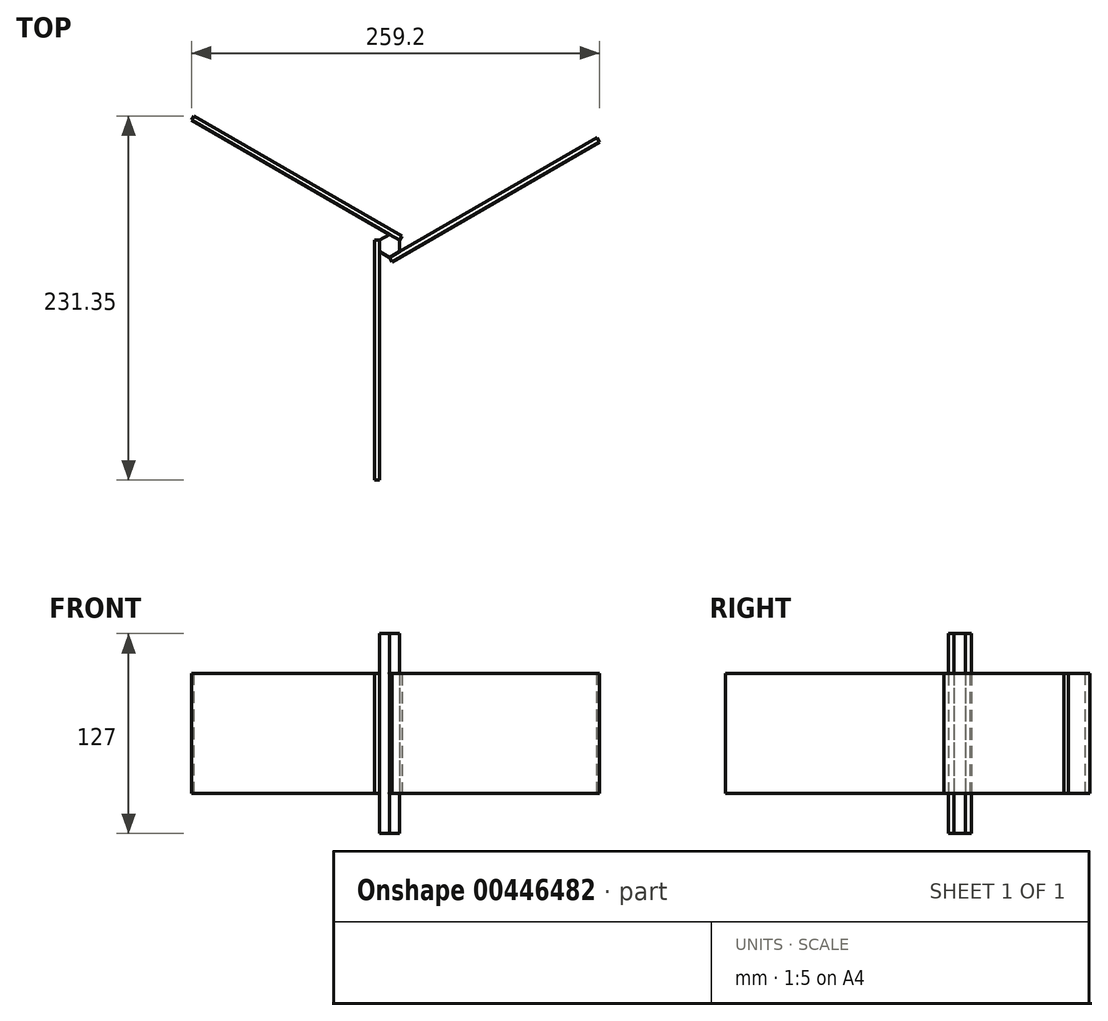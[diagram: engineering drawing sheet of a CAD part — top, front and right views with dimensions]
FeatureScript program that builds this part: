
annotation { "Feature Type Name" : "Feature", "Feature Type Description" : "" }
export const myFeature = defineFeature(function(context is Context, id is Id, definition is map)
    precondition{}
    {
        {
            var Q0;
            Q0=qCreatedBy(makeId("Top.planeOp"),FACE);
            var sketch = newSketch(context, id + "F0", { "sketchPlane" : qUnion([Q0])});
            skCircle(sketch, "E0.cCircle", {"center": v(0, 0) * mm, "radius": 6.35 * mm, "construction": true});
            skLineSegment(sketch, "E0.0", {"start": v(6.35, 3.67) * mm, "end": v(6.35, -3.67) * mm});
            skLineSegment(sketch, "E0.1", {"start": v(6.35, -3.67) * mm, "end": v(0, -7.33) * mm});
            skLineSegment(sketch, "E0.2", {"start": v(0, -7.33) * mm, "end": v(-6.35, -3.67) * mm});
            skLineSegment(sketch, "E0.3", {"start": v(-6.35, -3.67) * mm, "end": v(-6.35, 3.67) * mm});
            skLineSegment(sketch, "E0.4", {"start": v(-6.35, 3.67) * mm, "end": v(0, 7.33) * mm});
            skLineSegment(sketch, "E0.5", {"start": v(0, 7.33) * mm, "end": v(6.35, 3.67) * mm});
            skPoint(sketch, "E0.0.midPoint", {"position": v(6.35, 0) * mm});
            skSolve(sketch);
        }
        {
            var Q0;
            Q0=makeQuery(id+"F0.imprint","IMPRINT",FACE,{"disambiguationData":[TD([[makeQuery(id+"F0.imprint","IMPRINT",EDGE,{"derivedFrom":sQuery(id+"F0.wireOp",EDGE,"E0.0")}),-1.0]])]});
            extrude(context, id + "F1", {"entities" : qUnion([Q0]), "depth" : 127 * mm, "symmetric" : true});
        }
        {
            var Q0;
            Q0=makeQuery(id+"F1.opExtrude","SWEPT_FACE",FACE,{"disambiguationData":[OSD([sQuery(id+"F0.wireOp",EDGE,"E0.1")])]});
            var sketch = newSketch(context, id + "F2", { "sketchPlane" : qUnion([Q0])});
            skLineSegment(sketch, "E1.bottom", {"start": v(-3.67, -38.1) * mm, "end": v(148.73, -38.1) * mm});
            skLineSegment(sketch, "E1.top", {"start": v(-3.67, 38.1) * mm, "end": v(148.73, 38.1) * mm});
            skLineSegment(sketch, "E1.left", {"start": v(-3.67, -38.1) * mm, "end": v(-3.67, 38.1) * mm});
            skLineSegment(sketch, "E1.right", {"start": v(148.73, -38.1) * mm, "end": v(148.73, 38.1) * mm});
            skSolve(sketch);
        }
        {
            var Q0;
            {var subQ0=sQuery(id+"F2.wireOp",EDGE,"E1.right");Q0=makeQuery(id+"F2.imprint","IMPRINT",FACE,{"disambiguationData":[TD([[makeQuery(id+"F2.imprint","IMPRINT",EDGE,{"derivedFrom":subQ0}),1.0]])]});}
            var Q1;
            {var subQ0=sQuery(id+"F2.wireOp",EDGE,"E1.left");Q1=makeQuery(id+"F2.imprint","IMPRINT",FACE,{"disambiguationData":[TD([[makeQuery(id+"F2.imprint","IMPRINT",EDGE,{"derivedFrom":subQ0}),1.0]])]});}
            extrude(context, id + "F3", {"entities" : qUnion([Q0, Q1]), "depth" : 3.17 * mm});
        }
        {
            var Q0;
            Q0=qCreatedBy(makeId("Right.planeOp"),FACE);
            var sketch = newSketch(context, id + "F4", { "sketchPlane" : qUnion([Q0])});
            skLineSegment(sketch, "E2", {"start": v(0, 48.5) * mm, "end": v(0, -34.53) * mm});
            skSolve(sketch);
        }
        {
            var Q0;
            Q0=makeQuery(id+"F3.opExtrude","SWEPT_BODY",BODY,{"disambiguationData":[OSD([sQuery(id+"F2.wireOp",EDGE,"E1.bottom"),sQuery(id+"F2.wireOp",EDGE,"E1.top"),sQuery(id+"F2.wireOp",EDGE,"E1.left"),sQuery(id+"F2.wireOp",EDGE,"E1.right")])]});
            var Q1;
            Q1=sQuery(id+"F4.wireOp",EDGE,"E2");
            circularPattern(context, id + "F5", {"entities" : qUnion([Q0]), "axis" : qUnion([Q1]), "angle" : 360 * degree, "instanceCount" : 3, "equalSpace" : true, "computeTransformsWithoutBuiltin" : true});
        }
    });
